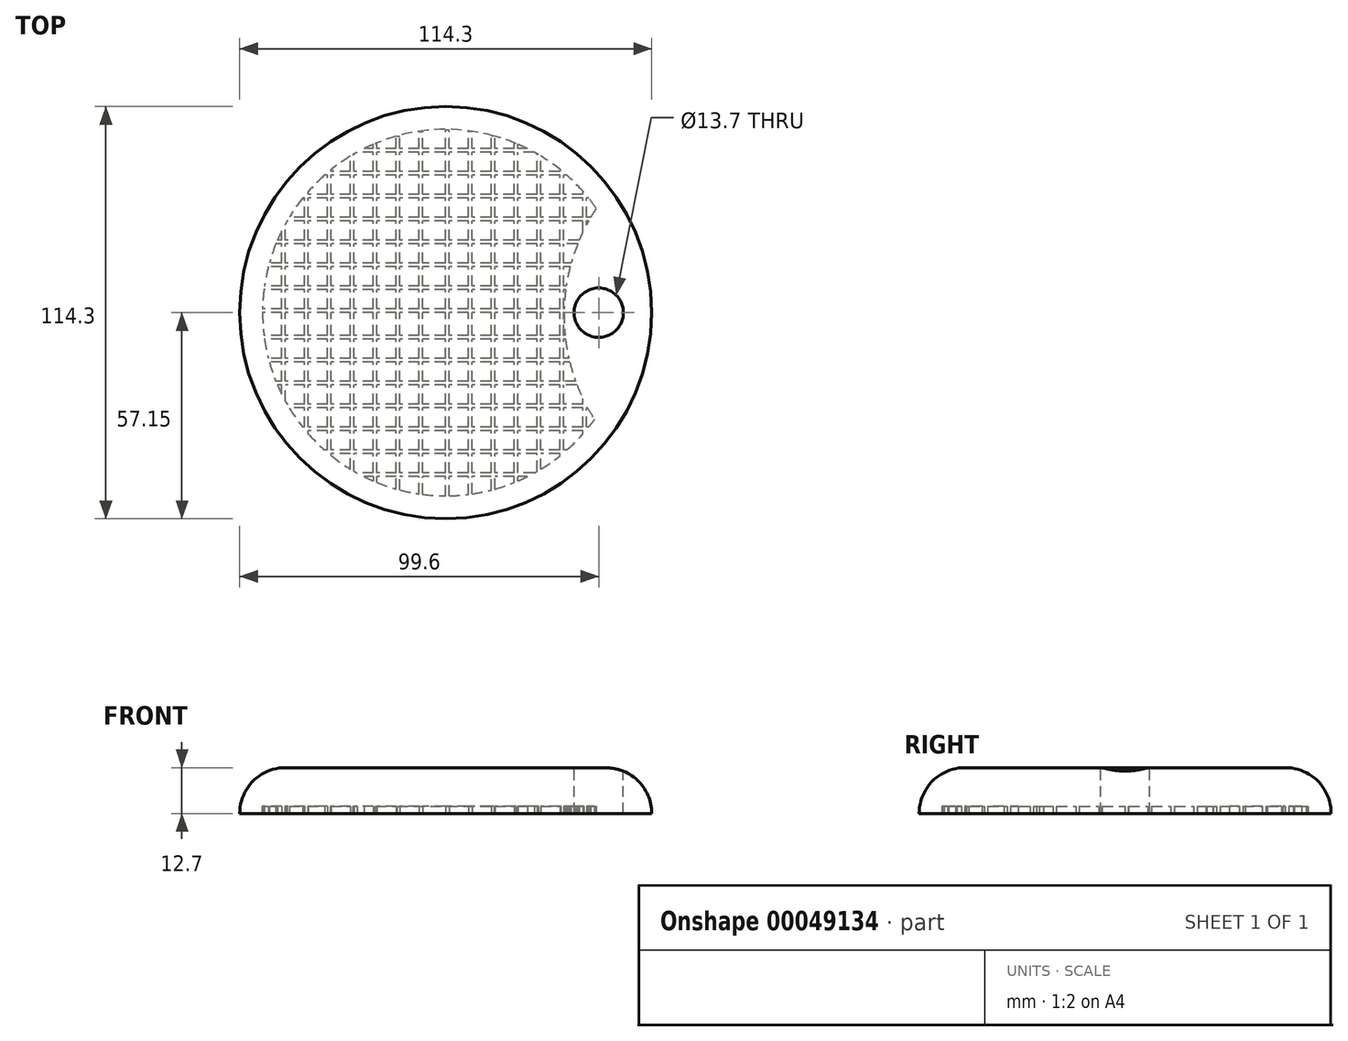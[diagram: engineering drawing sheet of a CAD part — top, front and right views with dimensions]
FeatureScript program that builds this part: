
annotation { "Feature Type Name" : "Feature", "Feature Type Description" : "" }
export const myFeature = defineFeature(function(context is Context, id is Id, definition is map)
    precondition{}
    {
        {
            var Q0;
            Q0=qCreatedBy(makeId("Top.planeOp"),FACE);
            var sketch = newSketch(context, id + "F0", { "sketchPlane" : qUnion([Q0])});
            skCircle(sketch, "E0", {"center": v(0, 0) * mm, "radius": 57.15 * mm});
            skSolve(sketch);
        }
        {
            var Q0;
            Q0=makeQuery(id+"F0.imprint","IMPRINT",FACE,{"disambiguationData":[TD([[makeQuery(id+"F0.imprint","IMPRINT",EDGE,{"derivedFrom":sQuery(id+"F0.wireOp",EDGE,"E0")}),1.0]])]});
            extrude(context, id + "F1", {"entities" : qUnion([Q0]), "depth" : 12.7 * mm});
        }
        {
            var Q0;
            Q0=makeQuery(id+"F1.opExtrude","CAP_EDGE",EDGE,{"disambiguationData":[OSD([sQuery(id+"F0.wireOp",EDGE,"E0")])],"isStart":false});
            fillet(context, id + "F2", {"entities" : qUnion([Q0]), "radius" : 12.7 * mm, "tangentPropagation" : true, "allowEdgeOverflow" : false});
        }
        {
            var Q0;
            Q0=makeQuery(id+"F1.opExtrude","CAP_FACE",FACE,{"disambiguationData":[OSD([sQuery(id+"F0.wireOp",EDGE,"E0")])],"isStart":true});
            var sketch = newSketch(context, id + "F3", { "sketchPlane" : qUnion([Q0])});
            skArc(sketch, "E1", {"start": v(41.29, 29.6) * mm, "mid": v(-50.8, -0.43) * mm, "end": v(41.78, -28.9) * mm});
            skArc(sketch, "E2", {"start": v(41.29, 29.6) * mm, "mid": v(32.82, 0.28) * mm, "end": v(41.78, -28.9) * mm});
            skSolve(sketch);
        }
        {
            var Q0;
            Q0 = qSketchRegion(id + "F3", true);
            extrude(context, id + "F4", {"entities" : qUnion([Q0]), "operationType" : NewBodyOperationType.REMOVE, "oppositeDirection" : true, "depth" : 2 * mm});
        }
        {
            var Q0;
            Q0=makeQuery(id+"F1.opExtrude","CAP_FACE",FACE,{"disambiguationData":[OSD([sQuery(id+"F0.wireOp",EDGE,"E0")])],"isStart":false});
            var sketch = newSketch(context, id + "F5", { "sketchPlane" : qUnion([Q0])});
            skCircle(sketch, "E3", {"center": v(42.45, 0) * mm, "radius": 6.35 * mm, "construction": true});
            skCircle(sketch, "E4", {"center": v(42.45, 0) * mm, "radius": 6.85 * mm});
            skSolve(sketch);
        }
        {
            var Q0;
            Q0=makeQuery(id+"F1.opExtrude","CAP_FACE",FACE,{"disambiguationData":[OSD([sQuery(id+"F0.wireOp",EDGE,"E0")])],"isStart":true});
            var sketch = newSketch(context, id + "F6", { "sketchPlane" : qUnion([Q0])});
            skLineSegment(sketch, "E5.bottom", {"start": v(-50.8, 0) * mm, "end": v(50.86, 0) * mm});
            skLineSegment(sketch, "E5.top", {"start": v(-50.8, -1) * mm, "end": v(50.86, -1) * mm});
            skLineSegment(sketch, "E5.left", {"start": v(-50.8, 0) * mm, "end": v(-50.8, -1) * mm});
            skLineSegment(sketch, "E5.right", {"start": v(50.86, 0) * mm, "end": v(50.86, -1) * mm});
            skLineSegment(sketch, "E6.top", {"start": v(-47.1, 19.05) * mm, "end": v(47.1, 19.05) * mm});
            skLineSegment(sketch, "E6.bottom", {"start": v(-47.1, 20.05) * mm, "end": v(47.1, 20.05) * mm});
            skLineSegment(sketch, "E7.top", {"start": v(-49.19, 12.7) * mm, "end": v(49.19, 12.7) * mm});
            skLineSegment(sketch, "E7.bottom", {"start": v(-49.19, 13.7) * mm, "end": v(49.19, 13.7) * mm});
            skLineSegment(sketch, "E6.right", {"start": v(47.1, 20.05) * mm, "end": v(47.1, 19.05) * mm});
            skLineSegment(sketch, "E6.left", {"start": v(-47.1, 20.05) * mm, "end": v(-47.1, 19.05) * mm});
            skLineSegment(sketch, "E7.right", {"start": v(49.19, 13.7) * mm, "end": v(49.19, 12.7) * mm});
            skLineSegment(sketch, "E7.left", {"start": v(-49.19, 13.7) * mm, "end": v(-49.19, 12.7) * mm});
            skLineSegment(sketch, "E8.bottom", {"start": v(-44, 26.4) * mm, "end": v(44, 26.4) * mm});
            skLineSegment(sketch, "E8.top", {"start": v(-44, 25.4) * mm, "end": v(44, 25.4) * mm});
            skLineSegment(sketch, "E9.bottom", {"start": v(-39.7, 32.75) * mm, "end": v(39.66, 32.75) * mm});
            skLineSegment(sketch, "E9.top", {"start": v(-39.7, 31.75) * mm, "end": v(39.66, 31.75) * mm});
            skLineSegment(sketch, "E8.left", {"start": v(-44, 26.4) * mm, "end": v(-44, 25.4) * mm});
            skLineSegment(sketch, "E8.right", {"start": v(44, 26.4) * mm, "end": v(44, 25.4) * mm});
            skLineSegment(sketch, "E9.left", {"start": v(-39.7, 32.75) * mm, "end": v(-39.7, 31.75) * mm});
            skLineSegment(sketch, "E9.right", {"start": v(39.66, 32.75) * mm, "end": v(39.66, 31.75) * mm});
            skLineSegment(sketch, "E10.top", {"start": v(-50.4, -7.35) * mm, "end": v(50.21, -7.35) * mm});
            skLineSegment(sketch, "E11.top", {"start": v(-44, -26.4) * mm, "end": v(44, -26.4) * mm});
            skLineSegment(sketch, "E10.bottom", {"start": v(-50.4, -6.35) * mm, "end": v(50.21, -6.35) * mm});
            skLineSegment(sketch, "E11.bottom", {"start": v(-44, -25.4) * mm, "end": v(44, -25.4) * mm});
            skLineSegment(sketch, "E12.bottom", {"start": v(-39.76, -31.75) * mm, "end": v(39.66, -31.75) * mm});
            skLineSegment(sketch, "E12.top", {"start": v(-39.76, -32.75) * mm, "end": v(39.66, -32.75) * mm});
            skLineSegment(sketch, "E13.bottom", {"start": v(-47.1, -19.05) * mm, "end": v(47.1, -19.05) * mm});
            skLineSegment(sketch, "E13.top", {"start": v(-47.1, -20.05) * mm, "end": v(47.1, -20.05) * mm});
            skLineSegment(sketch, "E11.left", {"start": v(-44, -25.4) * mm, "end": v(-44, -26.4) * mm});
            skLineSegment(sketch, "E12.left", {"start": v(-39.76, -31.75) * mm, "end": v(-39.76, -32.75) * mm});
            skLineSegment(sketch, "E11.right", {"start": v(44, -25.4) * mm, "end": v(44, -26.4) * mm});
            skLineSegment(sketch, "E12.right", {"start": v(39.66, -31.75) * mm, "end": v(39.66, -32.75) * mm});
            skLineSegment(sketch, "E13.right", {"start": v(47.1, -19.05) * mm, "end": v(47.1, -20.05) * mm});
            skLineSegment(sketch, "E10.right", {"start": v(50.21, -6.35) * mm, "end": v(50.21, -7.35) * mm});
            skLineSegment(sketch, "E10.left", {"start": v(-50.4, -6.35) * mm, "end": v(-50.4, -7.35) * mm});
            skLineSegment(sketch, "E13.left", {"start": v(-47.1, -19.05) * mm, "end": v(-47.1, -20.05) * mm});
            skLineSegment(sketch, "E14.top", {"start": v(-24.6, -45.45) * mm, "end": v(24.6, -45.45) * mm});
            skLineSegment(sketch, "E14.bottom", {"start": v(-24.6, -44.45) * mm, "end": v(24.6, -44.45) * mm});
            skLineSegment(sketch, "E14.right", {"start": v(-24.6, -44.45) * mm, "end": v(-24.6, -45.45) * mm});
            skLineSegment(sketch, "E14.left", {"start": v(24.6, -44.45) * mm, "end": v(24.6, -45.45) * mm});
            skLineSegment(sketch, "E15.top", {"start": v(-24.6, 44.45) * mm, "end": v(24.86, 44.45) * mm});
            skLineSegment(sketch, "E15.bottom", {"start": v(-24.6, 45.45) * mm, "end": v(24.86, 45.45) * mm});
            skLineSegment(sketch, "E15.right", {"start": v(-24.6, 45.45) * mm, "end": v(-24.6, 44.45) * mm});
            skLineSegment(sketch, "E15.left", {"start": v(24.86, 45.45) * mm, "end": v(24.86, 44.45) * mm});
            skLineSegment(sketch, "E16.top", {"start": v(-33.6, -39.1) * mm, "end": v(33.6, -39.1) * mm});
            skLineSegment(sketch, "E16.bottom", {"start": v(-33.6, -38.1) * mm, "end": v(33.6, -38.1) * mm});
            skLineSegment(sketch, "E16.left", {"start": v(33.6, -38.1) * mm, "end": v(33.6, -39.1) * mm});
            skLineSegment(sketch, "E16.right", {"start": v(-33.6, -38.1) * mm, "end": v(-33.6, -39.1) * mm});
            skLineSegment(sketch, "E17.top", {"start": v(-33.6, 38.1) * mm, "end": v(33.6, 38.1) * mm});
            skLineSegment(sketch, "E17.bottom", {"start": v(-33.6, 39.1) * mm, "end": v(33.6, 39.1) * mm});
            skLineSegment(sketch, "E17.left", {"start": v(33.6, 39.1) * mm, "end": v(33.6, 38.1) * mm});
            skLineSegment(sketch, "E17.right", {"start": v(-33.6, 39.1) * mm, "end": v(-33.6, 38.1) * mm});
            skLineSegment(sketch, "E18.bottom", {"start": v(-50.4, 7.35) * mm, "end": v(50.4, 7.35) * mm});
            skLineSegment(sketch, "E18.top", {"start": v(-50.4, 6.35) * mm, "end": v(50.4, 6.35) * mm});
            skLineSegment(sketch, "E18.right", {"start": v(50.4, 7.35) * mm, "end": v(50.4, 6.35) * mm});
            skLineSegment(sketch, "E18.left", {"start": v(-50.4, 7.35) * mm, "end": v(-50.4, 6.35) * mm});
            skLineSegment(sketch, "E19.top", {"start": v(-49.19, -13.7) * mm, "end": v(49.19, -13.7) * mm});
            skLineSegment(sketch, "E19.bottom", {"start": v(-49.19, -12.7) * mm, "end": v(49.19, -12.7) * mm});
            skLineSegment(sketch, "E19.left", {"start": v(-49.19, -12.7) * mm, "end": v(-49.19, -13.7) * mm});
            skLineSegment(sketch, "E19.right", {"start": v(49.19, -12.7) * mm, "end": v(49.19, -13.7) * mm});
            skSolve(sketch);
        }
        {
            var Q0;
            Q0 = qSketchRegion(id + "F6", true);
            var Q1;
            Q1=makeQuery(id+"F4.boolean.opBoolean","COPY",FACE,{"derivedFrom":makeQuery(id+"F4.opExtrude","CAP_FACE",FACE,{"disambiguationData":[OSD([sQuery(id+"F3.wireOp",EDGE,"E1")])],"isStart":false})});
            extrude(context, id + "F7", {"entities" : qUnion([Q0]), "operationType" : NewBodyOperationType.ADD, "endBound" : BoundingType.UP_TO_SURFACE, "oppositeDirection" : true, "endBoundEntityFace" : qUnion([Q1]), "depth" : 25 * mm});
        }
        {
            var Q0;
            Q0=makeQuery(id+"F7.boolean.opBoolean","MERGE",FACE,{"derivedFrom":[makeQuery(id+"F1.opExtrude","CAP_FACE",FACE,{"disambiguationData":[OSD([sQuery(id+"F0.wireOp",EDGE,"E0")])],"isStart":true}),makeQuery(id+"F7.opExtrude","CAP_FACE",FACE,{"disambiguationData":[OSD([sQuery(id+"F6.wireOp",EDGE,"E5.bottom"),sQuery(id+"F6.wireOp",EDGE,"E5.top"),sQuery(id+"F6.wireOp",EDGE,"E5.left"),sQuery(id+"F6.wireOp",EDGE,"E5.right")])],"isStart":true}),makeQuery(id+"F7.opExtrude","CAP_FACE",FACE,{"disambiguationData":[OSD([sQuery(id+"F6.wireOp",EDGE,"E6.top"),sQuery(id+"F6.wireOp",EDGE,"E6.bottom"),sQuery(id+"F6.wireOp",EDGE,"E6.right"),sQuery(id+"F6.wireOp",EDGE,"E6.left")])],"isStart":true}),makeQuery(id+"F7.opExtrude","CAP_FACE",FACE,{"disambiguationData":[OSD([sQuery(id+"F6.wireOp",EDGE,"E7.top"),sQuery(id+"F6.wireOp",EDGE,"E7.bottom"),sQuery(id+"F6.wireOp",EDGE,"E7.right"),sQuery(id+"F6.wireOp",EDGE,"E7.left")])],"isStart":true}),makeQuery(id+"F7.opExtrude","CAP_FACE",FACE,{"disambiguationData":[OSD([sQuery(id+"F6.wireOp",EDGE,"E8.bottom"),sQuery(id+"F6.wireOp",EDGE,"E8.top"),sQuery(id+"F6.wireOp",EDGE,"E8.left"),sQuery(id+"F6.wireOp",EDGE,"E8.right")])],"isStart":true}),makeQuery(id+"F7.opExtrude","CAP_FACE",FACE,{"disambiguationData":[OSD([sQuery(id+"F6.wireOp",EDGE,"E9.bottom"),sQuery(id+"F6.wireOp",EDGE,"E9.top"),sQuery(id+"F6.wireOp",EDGE,"E9.left"),sQuery(id+"F6.wireOp",EDGE,"E9.right")])],"isStart":true}),makeQuery(id+"F7.opExtrude","CAP_FACE",FACE,{"disambiguationData":[OSD([sQuery(id+"F6.wireOp",EDGE,"E10.top"),sQuery(id+"F6.wireOp",EDGE,"E10.bottom"),sQuery(id+"F6.wireOp",EDGE,"E10.right"),sQuery(id+"F6.wireOp",EDGE,"E10.left")])],"isStart":true}),makeQuery(id+"F7.opExtrude","CAP_FACE",FACE,{"disambiguationData":[OSD([sQuery(id+"F6.wireOp",EDGE,"E11.top"),sQuery(id+"F6.wireOp",EDGE,"E11.bottom"),sQuery(id+"F6.wireOp",EDGE,"E11.left"),sQuery(id+"F6.wireOp",EDGE,"E11.right")])],"isStart":true}),makeQuery(id+"F7.opExtrude","CAP_FACE",FACE,{"disambiguationData":[OSD([sQuery(id+"F6.wireOp",EDGE,"E12.bottom"),sQuery(id+"F6.wireOp",EDGE,"E12.top"),sQuery(id+"F6.wireOp",EDGE,"E12.left"),sQuery(id+"F6.wireOp",EDGE,"E12.right")])],"isStart":true}),makeQuery(id+"F7.opExtrude","CAP_FACE",FACE,{"disambiguationData":[OSD([sQuery(id+"F6.wireOp",EDGE,"E13.bottom"),sQuery(id+"F6.wireOp",EDGE,"E13.top"),sQuery(id+"F6.wireOp",EDGE,"E13.right"),sQuery(id+"F6.wireOp",EDGE,"E13.left")])],"isStart":true}),makeQuery(id+"F7.opExtrude","CAP_FACE",FACE,{"disambiguationData":[OSD([sQuery(id+"F6.wireOp",EDGE,"E14.top"),sQuery(id+"F6.wireOp",EDGE,"E14.bottom"),sQuery(id+"F6.wireOp",EDGE,"E14.right"),sQuery(id+"F6.wireOp",EDGE,"E14.left")])],"isStart":true}),makeQuery(id+"F7.opExtrude","CAP_FACE",FACE,{"disambiguationData":[OSD([sQuery(id+"F6.wireOp",EDGE,"E15.top"),sQuery(id+"F6.wireOp",EDGE,"E15.bottom"),sQuery(id+"F6.wireOp",EDGE,"E15.right"),sQuery(id+"F6.wireOp",EDGE,"E15.left")])],"isStart":true}),makeQuery(id+"F7.opExtrude","CAP_FACE",FACE,{"disambiguationData":[OSD([sQuery(id+"F6.wireOp",EDGE,"E16.top"),sQuery(id+"F6.wireOp",EDGE,"E16.bottom"),sQuery(id+"F6.wireOp",EDGE,"E16.left"),sQuery(id+"F6.wireOp",EDGE,"E16.right")])],"isStart":true}),makeQuery(id+"F7.opExtrude","CAP_FACE",FACE,{"disambiguationData":[OSD([sQuery(id+"F6.wireOp",EDGE,"E17.top"),sQuery(id+"F6.wireOp",EDGE,"E17.bottom"),sQuery(id+"F6.wireOp",EDGE,"E17.left"),sQuery(id+"F6.wireOp",EDGE,"E17.right")])],"isStart":true}),makeQuery(id+"F7.opExtrude","CAP_FACE",FACE,{"disambiguationData":[OSD([sQuery(id+"F6.wireOp",EDGE,"E18.bottom"),sQuery(id+"F6.wireOp",EDGE,"E18.top"),sQuery(id+"F6.wireOp",EDGE,"E18.right"),sQuery(id+"F6.wireOp",EDGE,"E18.left")])],"isStart":true}),makeQuery(id+"F7.opExtrude","CAP_FACE",FACE,{"disambiguationData":[OSD([sQuery(id+"F6.wireOp",EDGE,"E19.top"),sQuery(id+"F6.wireOp",EDGE,"E19.bottom"),sQuery(id+"F6.wireOp",EDGE,"E19.left"),sQuery(id+"F6.wireOp",EDGE,"E19.right")])],"isStart":true})]});
            var sketch = newSketch(context, id + "F8", { "sketchPlane" : qUnion([Q0])});
            skLineSegment(sketch, "E20.left", {"start": v(44.42, -24.39) * mm, "end": v(44.42, 24.63) * mm});
            skLineSegment(sketch, "E21.left", {"start": v(-25.43, -43.79) * mm, "end": v(-25.43, 44.2) * mm});
            skLineSegment(sketch, "E20.right", {"start": v(45.42, -24.39) * mm, "end": v(45.42, 24.63) * mm});
            skLineSegment(sketch, "E21.right", {"start": v(-26.43, -43.79) * mm, "end": v(-26.43, 44.2) * mm});
            skLineSegment(sketch, "E22.left", {"start": v(-31.78, -39.45) * mm, "end": v(-31.78, 39.86) * mm});
            skLineSegment(sketch, "E23.left", {"start": v(-6.38, -50.2) * mm, "end": v(-6.38, 50.6) * mm});
            skLineSegment(sketch, "E24.left", {"start": v(25.37, -43.79) * mm, "end": v(25.37, 44.2) * mm});
            skLineSegment(sketch, "E23.right", {"start": v(-7.38, -50.2) * mm, "end": v(-7.38, 50.6) * mm});
            skLineSegment(sketch, "E24.right", {"start": v(26.37, -43.79) * mm, "end": v(26.37, 44.2) * mm});
            skLineSegment(sketch, "E22.right", {"start": v(-32.78, -39.45) * mm, "end": v(-32.78, 39.86) * mm});
            skLineSegment(sketch, "E25.left", {"start": v(31.72, -39.45) * mm, "end": v(31.72, 39.86) * mm});
            skLineSegment(sketch, "E26.left", {"start": v(-12.73, -48.98) * mm, "end": v(-12.73, 49.4) * mm});
            skLineSegment(sketch, "E27.left", {"start": v(-38.13, -33.4) * mm, "end": v(-38.13, 33.8) * mm});
            skLineSegment(sketch, "E26.right", {"start": v(-13.73, -48.98) * mm, "end": v(-13.73, 49.4) * mm});
            skLineSegment(sketch, "E27.right", {"start": v(-39.13, -33.4) * mm, "end": v(-39.13, 33.8) * mm});
            skLineSegment(sketch, "E25.right", {"start": v(32.72, -39.45) * mm, "end": v(32.72, 39.86) * mm});
            skLineSegment(sketch, "E28.left", {"start": v(-19.08, -46.88) * mm, "end": v(-19.08, 47.3) * mm});
            skLineSegment(sketch, "E29.left", {"start": v(-44.48, -24.39) * mm, "end": v(-44.48, 24.8) * mm});
            skLineSegment(sketch, "E30.left", {"start": v(38.07, -33.4) * mm, "end": v(38.07, 33.8) * mm});
            skLineSegment(sketch, "E29.right", {"start": v(-45.48, -24.39) * mm, "end": v(-45.48, 24.8) * mm});
            skLineSegment(sketch, "E28.right", {"start": v(-20.08, -46.88) * mm, "end": v(-20.08, 47.3) * mm});
            skLineSegment(sketch, "E30.right", {"start": v(39.07, -33.4) * mm, "end": v(39.07, 33.8) * mm});
            skLineSegment(sketch, "E31.left", {"start": v(19.02, -46.88) * mm, "end": v(19.02, 47.3) * mm});
            skLineSegment(sketch, "E31.right", {"start": v(20.02, -46.88) * mm, "end": v(20.02, 47.3) * mm});
            skLineSegment(sketch, "E32.left", {"start": v(-0.03, -50.6) * mm, "end": v(-0.03, 51) * mm});
            skLineSegment(sketch, "E32.right", {"start": v(0.97, -50.6) * mm, "end": v(0.97, 51) * mm});
            skLineSegment(sketch, "E33.left", {"start": v(6.32, -50.2) * mm, "end": v(6.32, 50.6) * mm});
            skLineSegment(sketch, "E33.right", {"start": v(7.32, -50.2) * mm, "end": v(7.32, 50.6) * mm});
            skLineSegment(sketch, "E34.left", {"start": v(12.67, -48.98) * mm, "end": v(12.67, 49.4) * mm});
            skLineSegment(sketch, "E34.right", {"start": v(13.67, -48.98) * mm, "end": v(13.67, 49.4) * mm});
            skLineSegment(sketch, "E20.top", {"start": v(44.42, 24.63) * mm, "end": v(45.42, 24.63) * mm});
            skLineSegment(sketch, "E21.top", {"start": v(-25.43, 44.2) * mm, "end": v(-26.43, 44.2) * mm});
            skLineSegment(sketch, "E23.bottom", {"start": v(-6.38, -50.2) * mm, "end": v(-7.38, -50.2) * mm});
            skLineSegment(sketch, "E24.bottom", {"start": v(25.37, -43.79) * mm, "end": v(26.37, -43.79) * mm});
            skLineSegment(sketch, "E22.bottom", {"start": v(-31.78, -39.45) * mm, "end": v(-32.78, -39.45) * mm});
            skLineSegment(sketch, "E23.top", {"start": v(-6.38, 50.6) * mm, "end": v(-7.38, 50.6) * mm});
            skLineSegment(sketch, "E24.top", {"start": v(25.37, 44.2) * mm, "end": v(26.37, 44.2) * mm});
            skLineSegment(sketch, "E22.top", {"start": v(-31.78, 39.86) * mm, "end": v(-32.78, 39.86) * mm});
            skLineSegment(sketch, "E26.bottom", {"start": v(-12.73, -48.98) * mm, "end": v(-13.73, -48.98) * mm});
            skLineSegment(sketch, "E25.bottom", {"start": v(31.72, -39.45) * mm, "end": v(32.72, -39.45) * mm});
            skLineSegment(sketch, "E27.bottom", {"start": v(-38.13, -33.4) * mm, "end": v(-39.13, -33.4) * mm});
            skLineSegment(sketch, "E26.top", {"start": v(-12.73, 49.4) * mm, "end": v(-13.73, 49.4) * mm});
            skLineSegment(sketch, "E25.top", {"start": v(31.72, 39.86) * mm, "end": v(32.72, 39.86) * mm});
            skLineSegment(sketch, "E27.top", {"start": v(-38.13, 33.8) * mm, "end": v(-39.13, 33.8) * mm});
            skLineSegment(sketch, "E28.bottom", {"start": v(-19.08, -46.88) * mm, "end": v(-20.08, -46.88) * mm});
            skLineSegment(sketch, "E29.bottom", {"start": v(-44.48, -24.39) * mm, "end": v(-45.48, -24.39) * mm});
            skLineSegment(sketch, "E30.bottom", {"start": v(38.07, -33.4) * mm, "end": v(39.07, -33.4) * mm});
            skLineSegment(sketch, "E28.top", {"start": v(-19.08, 47.3) * mm, "end": v(-20.08, 47.3) * mm});
            skLineSegment(sketch, "E29.top", {"start": v(-44.48, 24.8) * mm, "end": v(-45.48, 24.8) * mm});
            skLineSegment(sketch, "E30.top", {"start": v(38.07, 33.8) * mm, "end": v(39.07, 33.8) * mm});
            skLineSegment(sketch, "E21.bottom", {"start": v(-25.43, -43.79) * mm, "end": v(-26.43, -43.79) * mm});
            skLineSegment(sketch, "E20.bottom", {"start": v(44.42, -24.39) * mm, "end": v(45.42, -24.39) * mm});
            skLineSegment(sketch, "E31.top", {"start": v(19.02, 47.3) * mm, "end": v(20.02, 47.3) * mm});
            skLineSegment(sketch, "E32.bottom", {"start": v(-0.03, -50.6) * mm, "end": v(0.97, -50.6) * mm});
            skLineSegment(sketch, "E32.top", {"start": v(-0.03, 51) * mm, "end": v(0.97, 51) * mm});
            skLineSegment(sketch, "E33.bottom", {"start": v(6.32, -50.2) * mm, "end": v(7.32, -50.2) * mm});
            skLineSegment(sketch, "E33.top", {"start": v(6.32, 50.6) * mm, "end": v(7.32, 50.6) * mm});
            skLineSegment(sketch, "E34.bottom", {"start": v(12.67, -48.98) * mm, "end": v(13.67, -48.98) * mm});
            skLineSegment(sketch, "E34.top", {"start": v(12.67, 49.4) * mm, "end": v(13.67, 49.4) * mm});
            skLineSegment(sketch, "E31.bottom", {"start": v(19.02, -46.88) * mm, "end": v(20.02, -46.88) * mm});
            skSolve(sketch);
        }
        {
            var Q0;
            Q0 = qSketchRegion(id + "F8", true);
            var Q1;
            {var subQ0=sQuery(id+"F3.wireOp",EDGE,"E1");Q1=makeQuery(id+"F7.boolean.opBoolean","SPLIT",FACE,{"disambiguationData":[TD([makeQuery(id+"F7.opExtrude","SWEPT_FACE",FACE,{"disambiguationData":[OSD([sQuery(id+"F6.wireOp",EDGE,"E8.bottom")])]})])],"derivedFrom":makeQuery(id+"F4.boolean.opBoolean","COPY",FACE,{"derivedFrom":makeQuery(id+"F4.opExtrude","CAP_FACE",FACE,{"disambiguationData":[OSD([subQ0])],"isStart":false})})});}
            extrude(context, id + "F9", {"entities" : qUnion([Q0]), "operationType" : NewBodyOperationType.ADD, "endBound" : BoundingType.UP_TO_SURFACE, "oppositeDirection" : true, "endBoundEntityFace" : qUnion([Q1]), "depth" : 25 * mm});
        }
        {
            var Q0;
            Q0 = qSketchRegion(id + "F5", true);
            extrude(context, id + "F10", {"entities" : qUnion([Q0]), "operationType" : NewBodyOperationType.REMOVE, "endBound" : BoundingType.THROUGH_ALL, "oppositeDirection" : true, "depth" : 25 * mm});
        }
    });
